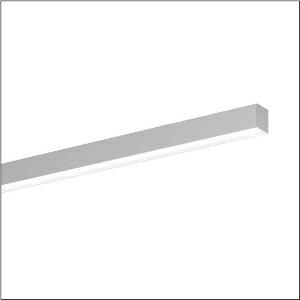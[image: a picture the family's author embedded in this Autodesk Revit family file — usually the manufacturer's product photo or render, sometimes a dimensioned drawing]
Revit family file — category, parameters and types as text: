
# Revit family: silica_21_51mx23db45sb
name_source: partatom
category: Lighting Fixtures
units: mm (PartAtom-declared; Revit-internal decimal feet)

## family parameters
Cut with Voids When Loaded = No
Host = Face
Light Source = No
Part Type = Normal
Room Calculation Point = No
Round Connector Dimension = Use Diameter
Shared = No

## types (1)
- --- (1 x LED, 4100 lm, 28.1 W, 4000K)
    Apparent Load = 28 VA
    CIE Flux Codes = 78 96 99 100 100
    Color Rendering = 80
    Color Temperature = 4000K
    Default Elevation = 1800 mm
    Description = Silica 21, office luminaire, primary optical cover: prismatic diffuser, of PMMA, CAT 2 (L<= 3000cd/m²), light emission: direct distribution, primary light characteristic: symmetric, installation type: surface-mounted, LED, rated luminous flux: 4.100lm, luminous efficacy: 146lm/W, light colour: 840, colour temperature: 4000K, control gear: DALI 2, with terminal, 3+2-pole, max. 2.5mm², mains connection: 220..240V, AC, 50/60Hz, rated input power: 28.1W, luminaire housing, of aluminium, metallic grey (RAL 9006), length: 1.504mm, width: 53mm, height: 53mm, protection rating (complete): IP20, insulation class (complete): insulation class I (protective earthing), certification: CE, permissible operating ambient temperature: 0..+35°C, standard: EN 50419, packaging unit: 1 piece
    Height = 53 mm
    Lamp = 1 x LED
    Lamp Light Flux = 4100 lm
    Lamp Power = 28.1 W
    Lamp count = 1
    Length = 1504 mm
    Luminous efficacy = 146 lm/W
    Manufacturer = Siteco
    ModVariant = No
    Model = 51MX23DB45SB
    Mounting Place = Ceiling
    Mounting Type = Surface mounted
    Number of Poles = 1
    OnlyDefault = Yes
    Power Factor = 1
    Product Name = Silica 21
    Product group = office luminaire | ceiling mounted
    ProductGroupID = 301
    Protection Class = Protection class I
    Protection Degree = IP 20
    RLX_Detail_Level = 1
    RLX_Emergency_Light_Flux = 0 lm
    RLX_Emergency_Type = 0
    RLX_Emergency_Type_DB = No
    RlxData = <blob elided: 21313 chars, md5=693710d5>
    Socket = socket
    Standby Power = 0 W
    System Light Flux = 4100 lm
    System Power = 28 W
    Type Comments = factory setting: luminous flux: 100 % | dim-lin: 254 | 323 mA
    Type Image = l_1335933.jpg
    URL = http://relux.com
    VarID = @adj_120977
    Voltage = 0 V
    Weight = 0.00 kg
    Width = 53 mm

## geometry (parser evidence)
native form markers: Blend x4, Sweep x12
no freeform markers — native parametric forms only
